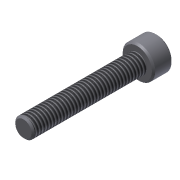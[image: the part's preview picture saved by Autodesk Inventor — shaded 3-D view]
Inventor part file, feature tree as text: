
AUTODESK INVENTOR PART (.ipt)
format: ipt  version: 2011 SP1 (Build 150282100, 282)  size: 105,984 bytes
history: native  units: in
note: dims shown in document units (in); Inventor stores cm internally (conversion verified against a paired STEP export)
features: extrude x3, sketch x3, thread x1, chamfer x1
ambient origin geometry x8: Origin, YZ Plane, XZ Plane, XY Plane, X Axis, Y Axis, Z Axis, Center Point
bodies: Solid1 (feature_tree)
feature tree (8):
  extrude  "Extrusion1"  Depth=1.378in TaperAngle=0.0deg
  extrude  "Extrusion2"  Depth=0.2362in TaperAngle=0.0deg
  extrude  "Extrusion3"  Depth=0.1181in TaperAngle=0.0deg
  thread  "Thread1"  [1 undecoded]
  chamfer  "Chamfer1"  Distance=0.02in Angle=45.0deg
  sketch  "Sketch1"  dims[d0=0.2362in d1=1.378in d2=0.0in]
  sketch  "Sketch2"  dims[d3=0.3937in d4=0.2362in d5=0.0in]
  sketch  "Sketch3"  dims[d6=0.1969in d7=0.1181in d8=0.0in d9=1.0in d10=0.0in d11=0.02in d12=0.125in d13=45.0deg]
note: 1 required parameter value undecoded (feature->parameter linkage not recoverable at this tier; creation-order binding heuristic only, values carry confidence <= 0.55)
